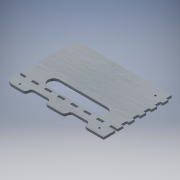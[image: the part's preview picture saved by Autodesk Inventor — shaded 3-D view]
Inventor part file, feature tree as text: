
AUTODESK INVENTOR PART (.ipt)
format: ipt  version: 2018.3 (Build 223284000, 284)  size: 2,430,976 bytes
history: native  units: mm
features: reference x12, other x5, extrude x4, sketch x4, fillet x2
ambient origin geometry x8: Origin, YZ Plane, XZ Plane, XY Plane, X Axis, Y Axis, Z Axis, Center Point
bodies: Solido1 (feature_tree)
feature tree (27):
  extrude  "Estrusione1"  Depth=80.0mm
  extrude  "Estrusione2"  Depth=4.0mm TaperAngle=0.0deg
  fillet  "Raccordo1"  Radius=4.0mm
  fillet  "Raccordo2"  Radius=15.0mm
  extrude  "Estrusione3"  Depth=10.0mm
  extrude  "Estrusione4"  Depth=3.3mm
  sketch  "Schizzo1"
  reference  "Riferimento14"
  reference  "Riferimento15"
  reference  "Riferimento16"
  reference  "Riferimento17"
  reference  "Riferimento18"
  reference  "Riferimento19"
  reference  "Riferimento20"
  reference  "Riferimento21"
  sketch  "Schizzo2"
  sketch  "Schizzo3"
  reference  "Riferimento22"
  reference  "Riferimento23"
  reference  "Riferimento24"
  reference  "Riferimento25"
  sketch  "Schizzo4"
  other  "Immagine1"
  other  "<userpath>\Desktop\Scorbot Hardware\Case Board V2\caseHw v2.iam"
  other  "caseHw v2.iam"
  other  "tavolaBase:1"
  other  "Dietro:1"
